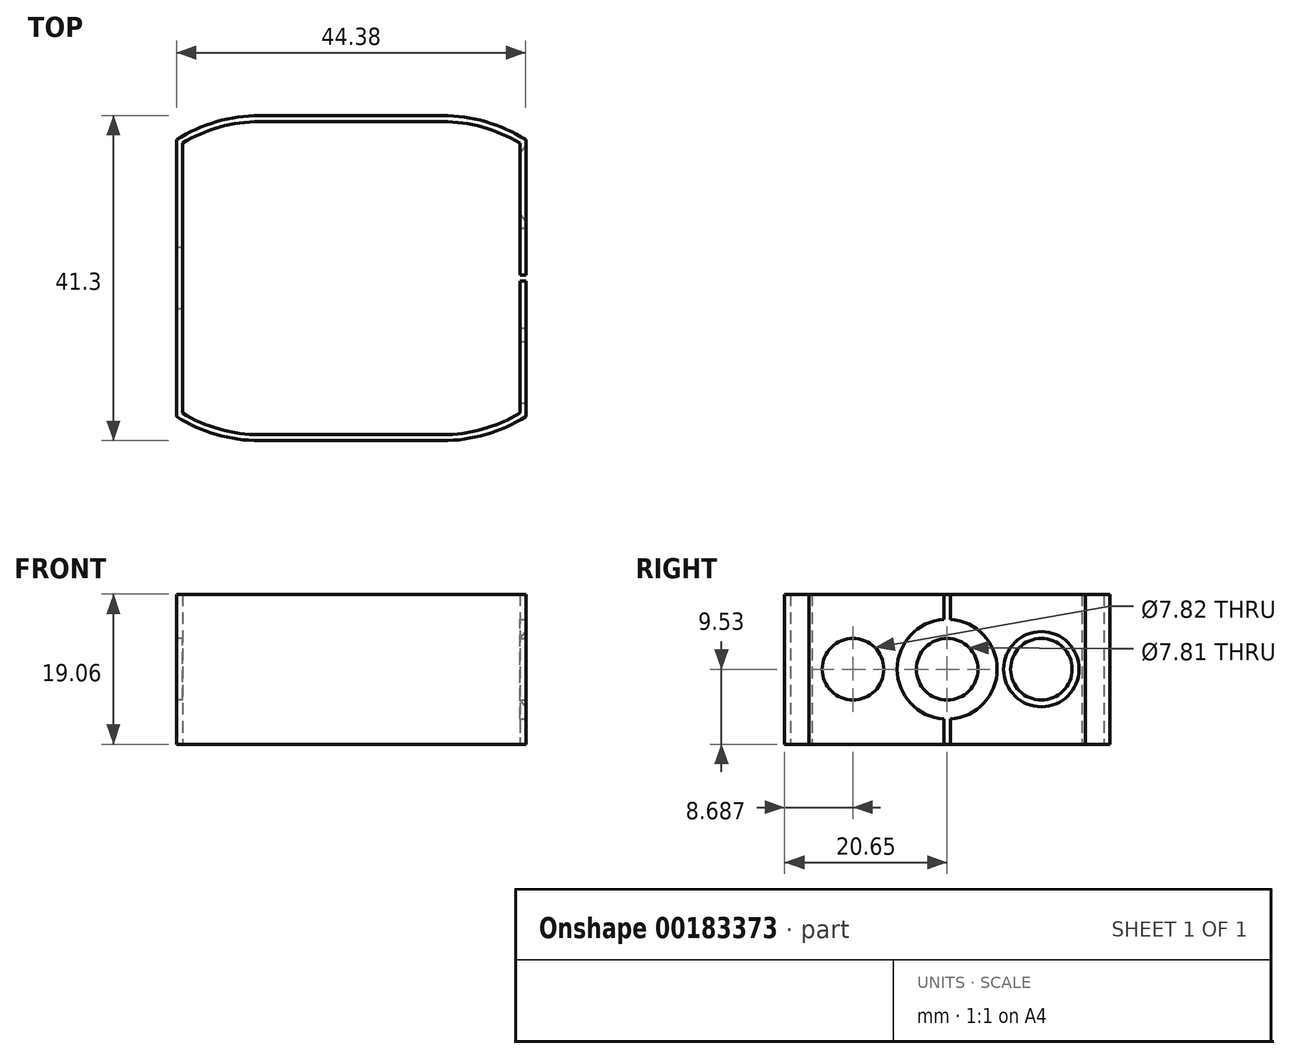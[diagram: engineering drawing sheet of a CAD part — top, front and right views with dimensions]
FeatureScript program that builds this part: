
annotation { "Feature Type Name" : "Feature", "Feature Type Description" : "" }
export const myFeature = defineFeature(function(context is Context, id is Id, definition is map)
    precondition{}
    {
        {
            var Q0;
            Q0=qCreatedBy(makeId("Top.planeOp"),FACE);
            var sketch = newSketch(context, id + "F0", { "sketchPlane" : qUnion([Q0])});
            skLineSegment(sketch, "E0.bottom", {"start": v(21.43, 17.15) * mm, "end": v(-21.43, 17.15) * mm});
            skLineSegment(sketch, "E0.top", {"start": v(21.43, -17.15) * mm, "end": v(-21.43, -17.14) * mm});
            skLineSegment(sketch, "E0.left", {"start": v(21.43, 17.14) * mm, "end": v(21.43, -17.15) * mm});
            skLineSegment(sketch, "E0.right", {"start": v(-21.43, 17.15) * mm, "end": v(-21.43, -17.15) * mm});
            skPoint(sketch, "E0.middle", {"position": v(0, 0) * mm});
            skLineSegment(sketch, "E1", {"start": v(-29.61, 0) * mm, "end": v(26.31, 0) * mm, "construction": true});
            skPoint(sketch, "E1.startSnap0", {"position": v(-21.43, 0) * mm});
            skLineSegment(sketch, "E2", {"start": v(-11.59, 19.88) * mm, "end": v(0, 19.88) * mm});
            skLineSegment(sketch, "E3", {"start": v(0, 19.88) * mm, "end": v(11.59, 19.88) * mm});
            skArc(sketch, "E4", {"start": v(-11.59, 19.88) * mm, "mid": v(-16.7, 19.19) * mm, "end": v(-21.43, 17.15) * mm});
            skArc(sketch, "E5", {"start": v(21.43, 17.14) * mm, "mid": v(16.7, 19.19) * mm, "end": v(11.59, 19.88) * mm});
            skArc(sketch, "E6.MirrorCS", {"start": v(-11.59, -19.88) * mm, "mid": v(-16.7, -19.19) * mm, "end": v(-21.43, -17.15) * mm});
            skLineSegment(sketch, "E7.MirrorCS", {"start": v(-11.59, -19.88) * mm, "end": v(0, -19.88) * mm});
            skLineSegment(sketch, "E8.MirrorCS", {"start": v(0, -19.88) * mm, "end": v(11.59, -19.88) * mm});
            skArc(sketch, "E9.MirrorCS", {"start": v(21.43, -17.15) * mm, "mid": v(16.7, -19.19) * mm, "end": v(11.59, -19.88) * mm});
            skLineSegment(sketch, "E10.0", {"start": v(-11.59, 20.65) * mm, "end": v(0, 20.65) * mm});
            skLineSegment(sketch, "E10.1", {"start": v(0, 20.65) * mm, "end": v(11.59, 20.65) * mm});
            skArc(sketch, "E10.2", {"start": v(-11.59, 20.65) * mm, "mid": v(-17.1, 19.86) * mm, "end": v(-22.2, 17.57) * mm});
            skArc(sketch, "E10.3", {"start": v(22.2, 17.57) * mm, "mid": v(17.1, 19.86) * mm, "end": v(11.59, 20.65) * mm});
            skLineSegment(sketch, "E10.4", {"start": v(22.2, 17.57) * mm, "end": v(22.2, -17.57) * mm});
            skArc(sketch, "E10.5", {"start": v(22.2, -17.57) * mm, "mid": v(17.1, -19.86) * mm, "end": v(11.59, -20.65) * mm});
            skLineSegment(sketch, "E10.6", {"start": v(-22.2, 17.57) * mm, "end": v(-22.2, -17.57) * mm});
            skArc(sketch, "E10.7", {"start": v(-11.59, -20.65) * mm, "mid": v(-17.1, -19.86) * mm, "end": v(-22.2, -17.57) * mm});
            skLineSegment(sketch, "E10.8", {"start": v(-11.59, -20.65) * mm, "end": v(0, -20.65) * mm});
            skLineSegment(sketch, "E10.9", {"start": v(0, -20.65) * mm, "end": v(11.59, -20.65) * mm});
            skSolve(sketch);
        }
        {
            var Q0;
            Q0=makeQuery(id+"F0.imprint","IMPRINT",FACE,{"disambiguationData":[TD([[makeQuery(id+"F0.imprint","IMPRINT",EDGE,{"derivedFrom":sQuery(id+"F0.wireOp",EDGE,"E0.left")}),1.0]])]});
            extrude(context, id + "F1", {"entities" : qUnion([Q0]), "endBound" : BoundingType.SYMMETRIC, "depth" : 19.05 * mm});
        }
        {
            var Q0;
            Q0=makeQuery(id+"F1.opExtrude","SWEPT_FACE",FACE,{"disambiguationData":[OSD([sQuery(id+"F0.wireOp",EDGE,"E10.4")])]});
            var sketch = newSketch(context, id + "F2", { "sketchPlane" : qUnion([Q0])});
            skCircle(sketch, "E11", {"center": v(0, 0) * mm, "radius": 6.35 * mm});
            skLineSegment(sketch, "E12.bottom", {"start": v(0.4, 16.24) * mm, "end": v(-0.4, 16.24) * mm});
            skLineSegment(sketch, "E12.top", {"start": v(0.4, -16.24) * mm, "end": v(-0.4, -16.24) * mm});
            skLineSegment(sketch, "E12.left", {"start": v(0.4, 16.24) * mm, "end": v(0.4, -16.24) * mm});
            skLineSegment(sketch, "E12.right", {"start": v(-0.4, 16.24) * mm, "end": v(-0.4, -16.24) * mm});
            skCircle(sketch, "E13", {"center": v(-11.96, 0) * mm, "radius": 3.9 * mm});
            skLineSegment(sketch, "E14", {"start": v(0, 20.34) * mm, "end": v(0, -24.58) * mm, "construction": true});
            skPoint(sketch, "E14.startSnap0", {"position": v(0, 9.53) * mm});
            skCircle(sketch, "E15.MirrorC", {"center": v(11.96, 0) * mm, "radius": 3.9 * mm});
            skSolve(sketch);
        }
        {
            var Q0;
            Q0=qSketchRegion(id+"F2",true);
            extrude(context, id + "F3", {"entities" : qUnion([Q0]), "operationType" : NewBodyOperationType.REMOVE, "oppositeDirection" : true, "depth" : 25.4 * mm});
        }
        {
            var Q0;
            Q0=qSketchRegion(id+"F2",true);
            extrude(context, id + "F4", {"entities" : qUnion([Q0]), "operationType" : NewBodyOperationType.REMOVE, "oppositeDirection" : true, "depth" : 25.4 * mm});
        }
        {
            var Q0;
            Q0=makeQuery(id+"F1.opExtrude","SWEPT_FACE",FACE,{"disambiguationData":[OSD([sQuery(id+"F0.wireOp",EDGE,"E10.6")])]});
            var sketch = newSketch(context, id + "F5", { "sketchPlane" : qUnion([Q0])});
            skCircle(sketch, "E16", {"center": v(0, 0) * mm, "radius": 3.9 * mm});
            skSolve(sketch);
        }
        {
            var Q0;
            Q0 = qSketchRegion(id + "F5", true);
            extrude(context, id + "F6", {"entities" : qUnion([Q0]), "operationType" : NewBodyOperationType.REMOVE, "oppositeDirection" : true, "depth" : 25.4 * mm});
        }
        {
            var Q0;
            Q0=makeQuery(id+"F3.boolean.opBoolean","COPY",EDGE,{"derivedFrom":makeQuery(id+"F3.opExtrude","CAP_EDGE",EDGE,{"disambiguationData":[OSD([sQuery(id+"F2.wireOp",EDGE,"E13")])],"isStart":true})});
            var Q1;
            Q1=makeQuery(id+"F3.boolean.opBoolean","COPY",EDGE,{"derivedFrom":makeQuery(id+"F3.opExtrude","CAP_EDGE",EDGE,{"disambiguationData":[OSD([sQuery(id+"F2.wireOp",EDGE,"E15.MirrorC")])],"isStart":true})});
            var Q2;
            Q2=makeQuery(id+"F6.boolean.opBoolean","COPY",EDGE,{"derivedFrom":makeQuery(id+"F6.opExtrude","CAP_EDGE",EDGE,{"disambiguationData":[OSD([sQuery(id+"F5.wireOp",EDGE,"E16")])],"isStart":true})});
            chamfer(context, id + "F7", {"entities" : qUnion([Q0, Q1, Q2]), "chamferType" : ChamferType.OFFSET_ANGLE, "width" : 0.76 * mm, "oppositeDirection" : false, "angle" : 49 * degree, "tangentPropagation" : true});
        }
    });
